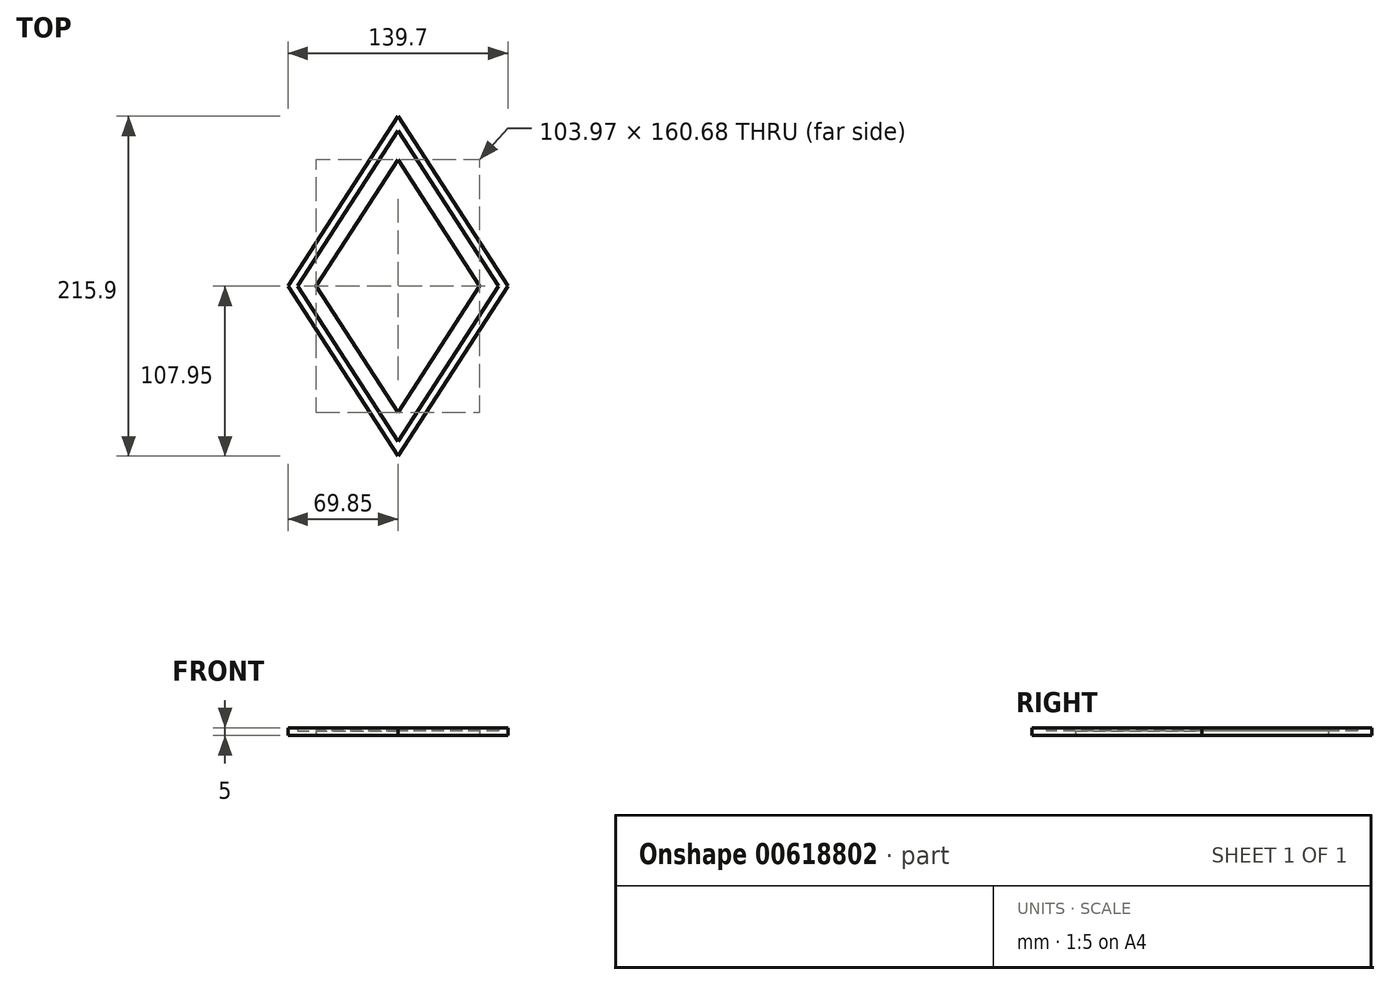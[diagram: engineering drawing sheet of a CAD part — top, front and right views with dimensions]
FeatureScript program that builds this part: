
annotation { "Feature Type Name" : "Feature", "Feature Type Description" : "" }
export const myFeature = defineFeature(function(context is Context, id is Id, definition is map)
    precondition{}
    {
        {
            var Q0;
            Q0=qCreatedBy(makeId("Top.planeOp"),FACE);
            var sketch = newSketch(context, id + "F0", { "sketchPlane" : qUnion([Q0])});
            skLineSegment(sketch, "E0.bottom", {"start": v(69.85, 107.95) * mm, "end": v(-69.85, 107.95) * mm, "construction": true});
            skLineSegment(sketch, "E0.left", {"start": v(69.85, 107.95) * mm, "end": v(69.85, -107.95) * mm, "construction": true});
            skLineSegment(sketch, "E0.right", {"start": v(-69.85, 107.95) * mm, "end": v(-69.85, -107.95) * mm, "construction": true});
            skPoint(sketch, "E0.middle", {"position": v(0, 0) * mm});
            skLineSegment(sketch, "E1", {"start": v(0, 0) * mm, "end": v(0, 107.95) * mm, "construction": true});
            skLineSegment(sketch, "E2", {"start": v(-69.85, -107.95) * mm, "end": v(69.85, -107.95) * mm, "construction": true});
            skPoint(sketch, "E3", {"position": v(-69.85, 0) * mm});
            skPoint(sketch, "E4", {"position": v(69.85, 0) * mm});
            skPoint(sketch, "E5", {"position": v(0, -107.95) * mm});
            skLineSegment(sketch, "E6", {"start": v(-69.85, 0) * mm, "end": v(0, -107.95) * mm});
            skLineSegment(sketch, "E7", {"start": v(0, -107.95) * mm, "end": v(69.85, 0) * mm});
            skLineSegment(sketch, "E8", {"start": v(69.85, 0) * mm, "end": v(0, 107.95) * mm});
            skLineSegment(sketch, "E9", {"start": v(0, 107.95) * mm, "end": v(-69.85, 0) * mm});
            skLineSegment(sketch, "E10.0", {"start": v(-63.9, 0) * mm, "end": v(0, -98.75) * mm});
            skLineSegment(sketch, "E10.1", {"start": v(0, 98.75) * mm, "end": v(-63.9, 0) * mm});
            skLineSegment(sketch, "E10.2", {"start": v(63.9, 0) * mm, "end": v(0, 98.75) * mm});
            skLineSegment(sketch, "E10.3", {"start": v(0, -98.75) * mm, "end": v(63.9, 0) * mm});
            skLineSegment(sketch, "E11.0", {"start": v(0, 80.34) * mm, "end": v(-51.98, 0) * mm});
            skLineSegment(sketch, "E11.1", {"start": v(51.98, 0) * mm, "end": v(0, 80.34) * mm});
            skLineSegment(sketch, "E11.2", {"start": v(0, -80.34) * mm, "end": v(51.98, 0) * mm});
            skLineSegment(sketch, "E11.3", {"start": v(-51.98, 0) * mm, "end": v(0, -80.34) * mm});
            skLineSegment(sketch, "E12", {"start": v(-69.85, 0) * mm, "end": v(-63.9, 0) * mm});
            skSolve(sketch);
        }
        {
            var Q0;
            Q0=makeQuery(id+"F0.imprint","IMPRINT",FACE,{"disambiguationData":[TD([[makeQuery(id+"F0.imprint","IMPRINT",EDGE,{"derivedFrom":sQuery(id+"F0.wireOp",EDGE,"E6")}),1.0]])]});
            extrude(context, id + "F1", {"entities" : qUnion([Q0]), "depth" : 5 * mm, "offsetDistance" : 25 * mm});
        }
        {
            var Q0;
            Q0=makeQuery(id+"F0.imprint","IMPRINT",FACE,{"disambiguationData":[TD([[makeQuery(id+"F0.imprint","IMPRINT",EDGE,{"derivedFrom":sQuery(id+"F0.wireOp",EDGE,"E10.0")}),1.0]])]});
            extrude(context, id + "F2", {"entities" : qUnion([Q0]), "operationType" : NewBodyOperationType.ADD, "depth" : 3 * mm, "offsetDistance" : 25 * mm});
        }
    });
